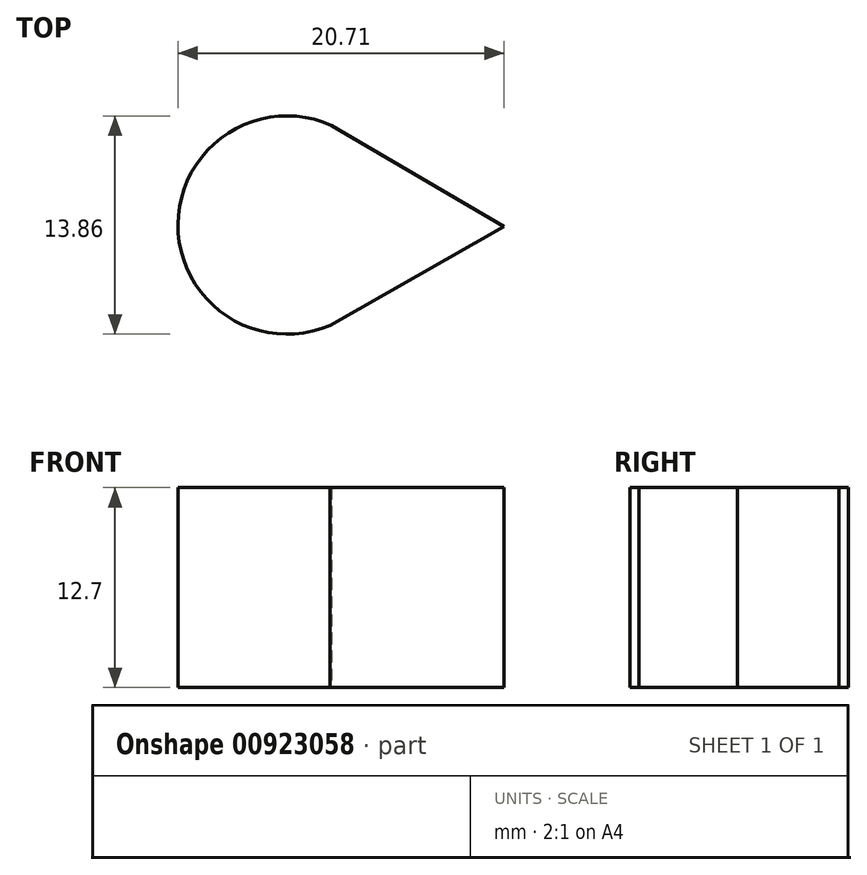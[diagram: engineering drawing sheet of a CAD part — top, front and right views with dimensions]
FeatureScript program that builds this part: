
annotation { "Feature Type Name" : "Feature", "Feature Type Description" : "" }
export const myFeature = defineFeature(function(context is Context, id is Id, definition is map)
    precondition{}
    {
        {
            var Q0;
            Q0=qCreatedBy(makeId("Top.planeOp"),FACE);
            var sketch = newSketch(context, id + "F0", { "sketchPlane" : qUnion([Q0])});
            skCircle(sketch, "E0.cCircle", {"center": v(0, 0) * mm, "radius": 7.33 * mm, "construction": true});
            skLineSegment(sketch, "E0.0", {"start": v(-3.71, -6.32) * mm, "end": v(-3.62, 6.38) * mm});
            skLineSegment(sketch, "E0.1", {"start": v(-3.62, 6.38) * mm, "end": v(7.33, -0.06) * mm});
            skLineSegment(sketch, "E0.2", {"start": v(7.33, -0.06) * mm, "end": v(-3.71, -6.32) * mm});
            skArc(sketch, "E1", {"start": v(-3.71, -6.32) * mm, "mid": v(-13.33, 0.87) * mm, "end": v(-2.3, 5.6) * mm});
            skSolve(sketch);
        }
        {
            var Q0;
            {var subQ0=sQuery(id+"F0.wireOp",EDGE,"E0.0");Q0=makeQuery(id+"F0.imprint","IMPRINT",FACE,{"disambiguationData":[TD([[makeQuery(id+"F0.imprint","IMPRINT",EDGE,{"derivedFrom":subQ0}),1.0]])]});}
            var Q1;
            {var subQ0=sQuery(id+"F0.wireOp",EDGE,"E0.0");Q1=makeQuery(id+"F0.imprint","IMPRINT",FACE,{"disambiguationData":[TD([[makeQuery(id+"F0.imprint","IMPRINT",EDGE,{"derivedFrom":subQ0}),-1.0]])]});}
            extrude(context, id + "F1", {"entities" : qUnion([Q0, Q1]), "depth" : 12.7 * mm, "offsetDistance" : 25.4 * mm});
        }
    });
